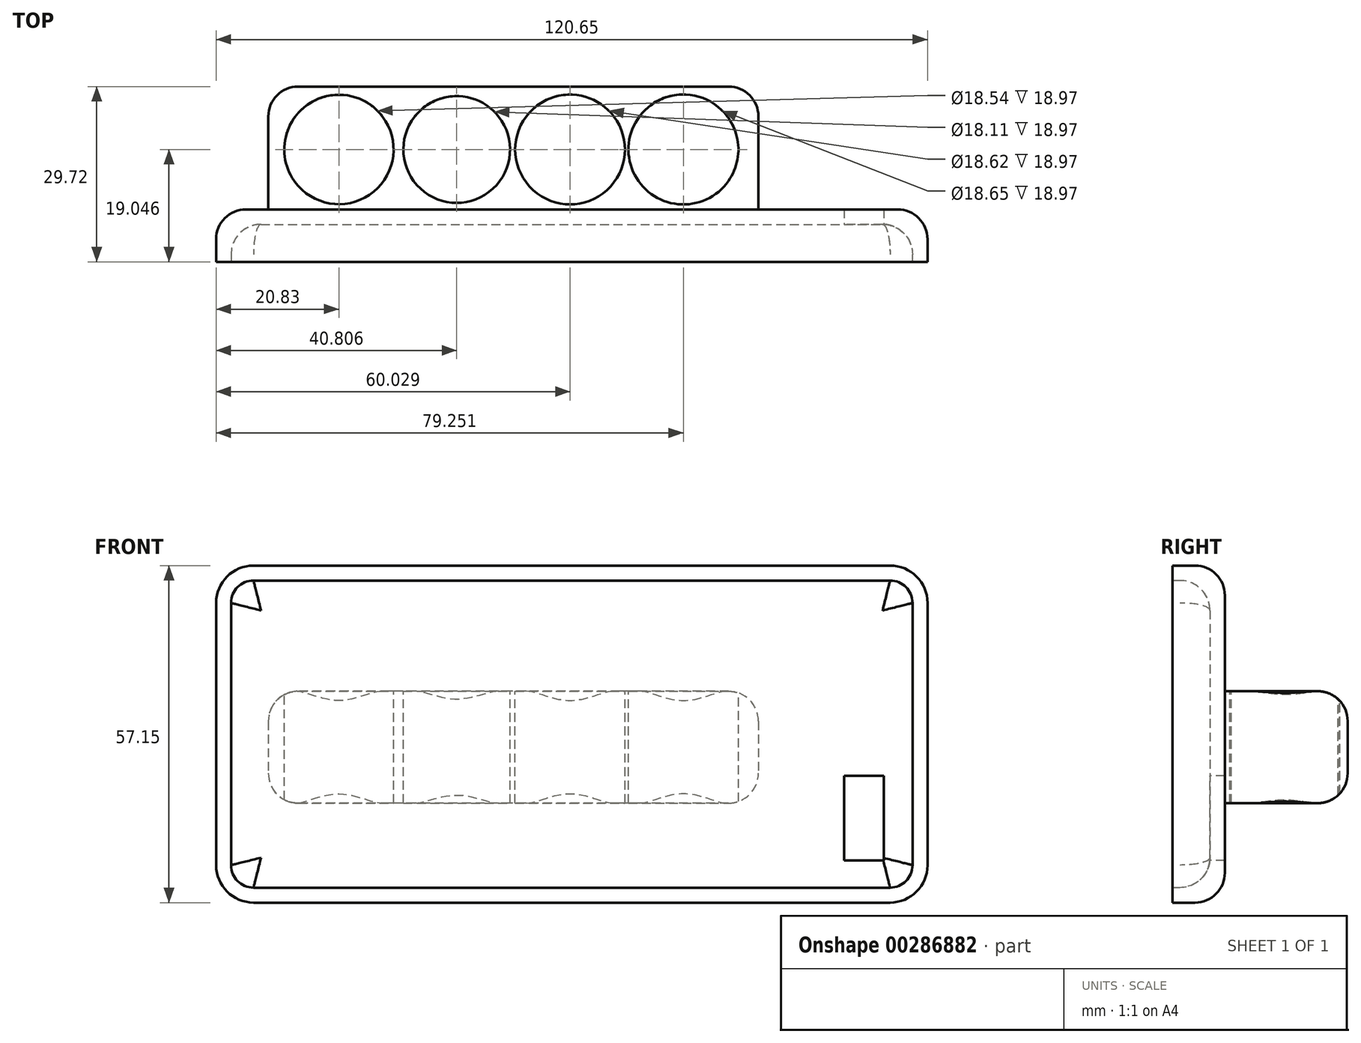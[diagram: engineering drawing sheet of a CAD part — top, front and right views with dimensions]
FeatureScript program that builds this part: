
annotation { "Feature Type Name" : "Feature", "Feature Type Description" : "" }
export const myFeature = defineFeature(function(context is Context, id is Id, definition is map)
    precondition{}
    {
        {
            var Q0;
            Q0=qCreatedBy(makeId("Front.planeOp"),FACE);
            var sketch = newSketch(context, id + "F0", { "sketchPlane" : qUnion([Q0])});
            skLineSegment(sketch, "E0.bottom", {"start": v(-56.78, 40.28) * mm, "end": v(51.17, 40.28) * mm});
            skLineSegment(sketch, "E0.top", {"start": v(-56.78, -16.87) * mm, "end": v(51.17, -16.87) * mm});
            skLineSegment(sketch, "E0.left", {"start": v(-63.13, 33.93) * mm, "end": v(-63.13, -10.52) * mm});
            skLineSegment(sketch, "E0.right", {"start": v(57.52, 33.93) * mm, "end": v(57.52, -10.52) * mm});
            skPoint(sketch, "E1.visualSharp", {"position": v(-63.13, 40.28) * mm});
            skArc(sketch, "E1.filletArc", {"start": v(-56.78, 40.28) * mm, "mid": v(-61.27, 38.42) * mm, "end": v(-63.13, 33.93) * mm});
            skPoint(sketch, "E2.visualSharp", {"position": v(57.52, 40.28) * mm});
            skArc(sketch, "E2.filletArc", {"start": v(57.52, 33.93) * mm, "mid": v(55.66, 38.42) * mm, "end": v(51.17, 40.28) * mm});
            skPoint(sketch, "E3.visualSharp", {"position": v(57.52, -16.87) * mm});
            skArc(sketch, "E3.filletArc", {"start": v(51.17, -16.87) * mm, "mid": v(55.66, -15) * mm, "end": v(57.52, -10.52) * mm});
            skPoint(sketch, "E4.visualSharp", {"position": v(-63.13, -16.87) * mm});
            skArc(sketch, "E4.filletArc", {"start": v(-63.13, -10.52) * mm, "mid": v(-61.27, -15) * mm, "end": v(-56.78, -16.87) * mm});
            skSolve(sketch);
        }
        {
            var Q0;
            Q0=makeQuery(id+"F0.imprint","IMPRINT",FACE,{"disambiguationData":[TD([[makeQuery(id+"F0.imprint","IMPRINT",EDGE,{"derivedFrom":sQuery(id+"F0.wireOp",EDGE,"E0.bottom")}),-1.0]])]});
            extrude(context, id + "F1", {"entities" : qUnion([Q0]), "oppositeDirection" : true, "depth" : 8.9 * mm});
        }
        {
            var Q0;
            Q0=makeQuery(id+"F1.opExtrude","CAP_FACE",FACE,{"disambiguationData":[OSD([sQuery(id+"F0.wireOp",EDGE,"E0.bottom"),sQuery(id+"F0.wireOp",EDGE,"E0.top"),sQuery(id+"F0.wireOp",EDGE,"E0.left"),sQuery(id+"F0.wireOp",EDGE,"E0.right"),sQuery(id+"F0.wireOp",EDGE,"E1.filletArc"),sQuery(id+"F0.wireOp",EDGE,"E2.filletArc"),sQuery(id+"F0.wireOp",EDGE,"E3.filletArc"),sQuery(id+"F0.wireOp",EDGE,"E4.filletArc")])],"isStart":true});
            shell(context, id + "F2", {"entities" : qUnion([Q0]), "thickness" : 2.54 * mm});
        }
        {
            var Q0;
            Q0=qCreatedBy(makeId("Front.planeOp"),FACE);
            var sketch = newSketch(context, id + "F3", { "sketchPlane" : qUnion([Q0])});
            skLineSegment(sketch, "E5.bottom", {"start": v(28.84, 18.97) * mm, "end": v(-54.28, 18.97) * mm});
            skLineSegment(sketch, "E5.top", {"start": v(28.84, 0) * mm, "end": v(-54.28, 0) * mm});
            skLineSegment(sketch, "E5.left", {"start": v(28.84, 18.97) * mm, "end": v(28.84, 0) * mm});
            skLineSegment(sketch, "E5.right", {"start": v(-54.28, 18.97) * mm, "end": v(-54.28, 0) * mm});
            skSolve(sketch);
        }
        {
            var Q0;
            Q0=makeQuery(id+"F3.imprint","IMPRINT",FACE,{"disambiguationData":[TD([[makeQuery(id+"F3.imprint","IMPRINT",EDGE,{"derivedFrom":sQuery(id+"F3.wireOp",EDGE,"E5.bottom")}),1.0]])]});
            extrude(context, id + "F4", {"entities" : qUnion([Q0]), "operationType" : NewBodyOperationType.ADD, "oppositeDirection" : true, "depth" : 29.72 * mm, "hasSecondDirection" : true, "secondDirectionOppositeDirection" : true, "secondDirectionDepth" : 8.13 * mm});
        }
        {
            var Q0;
            Q0=qCreatedBy(makeId("Top.planeOp"),FACE);
            var sketch = newSketch(context, id + "F5", { "sketchPlane" : qUnion([Q0])});
            skCircle(sketch, "E6", {"center": v(16.12, 19.05) * mm, "radius": 9.32 * mm});
            skCircle(sketch, "E7", {"center": v(-3.1, 19.05) * mm, "radius": 9.3 * mm});
            skCircle(sketch, "E8", {"center": v(-22.32, 19.05) * mm, "radius": 9.05 * mm});
            skCircle(sketch, "E9", {"center": v(-42.3, 19.05) * mm, "radius": 9.27 * mm});
            skSolve(sketch);
        }
        {
            var Q0;
            Q0=makeQuery(id+"F5.imprint","IMPRINT",FACE,{"disambiguationData":[TD([[makeQuery(id+"F5.imprint","IMPRINT",EDGE,{"derivedFrom":sQuery(id+"F5.wireOp",EDGE,"E6")}),1.0]])]});
            var Q1;
            Q1=makeQuery(id+"F5.imprint","IMPRINT",FACE,{"disambiguationData":[TD([[makeQuery(id+"F5.imprint","IMPRINT",EDGE,{"derivedFrom":sQuery(id+"F5.wireOp",EDGE,"E7")}),1.0]])]});
            var Q2;
            Q2=makeQuery(id+"F5.imprint","IMPRINT",FACE,{"disambiguationData":[TD([[makeQuery(id+"F5.imprint","IMPRINT",EDGE,{"derivedFrom":sQuery(id+"F5.wireOp",EDGE,"E8")}),1.0]])]});
            var Q3;
            Q3=makeQuery(id+"F5.imprint","IMPRINT",FACE,{"disambiguationData":[TD([[makeQuery(id+"F5.imprint","IMPRINT",EDGE,{"derivedFrom":sQuery(id+"F5.wireOp",EDGE,"E9")}),1.0]])]});
            extrude(context, id + "F6", {"entities" : qUnion([Q0, Q1, Q2, Q3]), "operationType" : NewBodyOperationType.REMOVE, "oppositeDirection" : true, "depth" : 25.4 * mm, "hasSecondDirection" : true, "secondDirectionOppositeDirection" : false, "secondDirectionDepth" : 31.75 * mm});
        }
        {
            var Q0;
            Q0=makeQuery(id+"F4.opExtrude","CAP_EDGE",EDGE,{"disambiguationData":[OSD([sQuery(id+"F3.wireOp",EDGE,"E5.top")])],"isStart":false});
            fillet(context, id + "F7", {"entities" : qUnion([Q0]), "radius" : 5.08 * mm, "tangentPropagation" : true, "allowEdgeOverflow" : false});
        }
        {
            var Q0;
            Q0=makeQuery(id+"F4.opExtrude","CAP_EDGE",EDGE,{"disambiguationData":[OSD([sQuery(id+"F3.wireOp",EDGE,"E5.bottom")])],"isStart":false});
            fillet(context, id + "F8", {"entities" : qUnion([Q0]), "radius" : 5.08 * mm, "tangentPropagation" : true, "allowEdgeOverflow" : false});
        }
        {
            var Q0;
            Q0=makeQuery(id+"F4.opExtrude","CAP_EDGE",EDGE,{"disambiguationData":[OSD([sQuery(id+"F3.wireOp",EDGE,"E5.left")])],"isStart":false});
            fillet(context, id + "F9", {"entities" : qUnion([Q0]), "radius" : 5.08 * mm, "tangentPropagation" : true, "allowEdgeOverflow" : false});
        }
        {
            var Q0;
            Q0=makeQuery(id+"F4.opExtrude","CAP_EDGE",EDGE,{"disambiguationData":[OSD([sQuery(id+"F3.wireOp",EDGE,"E5.right")])],"isStart":false});
            fillet(context, id + "F10", {"entities" : qUnion([Q0]), "radius" : 5.08 * mm, "tangentPropagation" : true, "allowEdgeOverflow" : false});
        }
        {
            var Q0;
            Q0=makeQuery(id+"F1.opExtrude","CAP_EDGE",EDGE,{"disambiguationData":[OSD([sQuery(id+"F0.wireOp",EDGE,"E0.bottom")])],"isStart":false});
            fillet(context, id + "F11", {"entities" : qUnion([Q0]), "radius" : 5.08 * mm, "tangentPropagation" : true, "allowEdgeOverflow" : false});
        }
        {
            var Q0;
            {var subQ0=sQuery(id+"F0.wireOp",EDGE,"E0.bottom");Q0=makeQuery(id+"F2.opShell","OFFSET_EDGE",EDGE,{"disambiguationData":[OSD([subQ0]),TDD([makeQuery(id+"F1.opExtrude","CAP_EDGE",EDGE,{"disambiguationData":[OSD([subQ0])],"isStart":false})])]});}
            fillet(context, id + "F12", {"entities" : qUnion([Q0]), "radius" : 5.08 * mm, "tangentPropagation" : true, "allowEdgeOverflow" : false});
        }
        {
            var Q0;
            Q0=qCreatedBy(makeId("Front.planeOp"),FACE);
            var sketch = newSketch(context, id + "F13", { "sketchPlane" : qUnion([Q0])});
            skLineSegment(sketch, "E10.bottom", {"start": v(50.12, -9.75) * mm, "end": v(43.37, -9.75) * mm});
            skLineSegment(sketch, "E10.top", {"start": v(50.12, 4.66) * mm, "end": v(43.37, 4.66) * mm});
            skLineSegment(sketch, "E10.left", {"start": v(50.12, -9.75) * mm, "end": v(50.12, 4.66) * mm});
            skLineSegment(sketch, "E10.right", {"start": v(43.37, -9.75) * mm, "end": v(43.37, 4.66) * mm});
            skSolve(sketch);
        }
        {
            var Q0;
            Q0=makeQuery(id+"F13.imprint","IMPRINT",FACE,{"disambiguationData":[TD([[makeQuery(id+"F13.imprint","IMPRINT",EDGE,{"derivedFrom":sQuery(id+"F13.wireOp",EDGE,"E10.bottom")}),-1.0]])]});
            extrude(context, id + "F14", {"entities" : qUnion([Q0]), "operationType" : NewBodyOperationType.REMOVE, "oppositeDirection" : true, "depth" : 25.4 * mm});
        }
        {
            var Q0;
            Q0=qCreatedBy(makeId("Right.planeOp"),FACE);
            var sketch = newSketch(context, id + "F15", { "sketchPlane" : qUnion([Q0])});
            skLineSegment(sketch, "E11.bottom", {"start": v(0, -9.62) * mm, "end": v(3.34, -9.62) * mm});
            skLineSegment(sketch, "E11.top", {"start": v(0, 0) * mm, "end": v(3.34, 0) * mm});
            skLineSegment(sketch, "E11.left", {"start": v(0, -9.62) * mm, "end": v(0, 0) * mm});
            skLineSegment(sketch, "E11.right", {"start": v(3.34, -9.62) * mm, "end": v(3.34, 0) * mm});
            skSolve(sketch);
        }
        {
            var Q0;
            Q0=sQuery(id+"F15.wireOp",EDGE,"E11.top");
            var Q1;
            Q1=sQuery(id+"F15.wireOp",EDGE,"E11.right");
            var Q2;
            Q2=sQuery(id+"F15.wireOp",EDGE,"E11.bottom");
            var Q3;
            Q3=sQuery(id+"F15.wireOp",EDGE,"E11.left");
            extrude(context, id + "F16", {"bodyType" : ToolBodyType.SURFACE, "surfaceEntities" : qUnion([Q0, Q1, Q2, Q3]), "depth" : 58.67 * mm, "hasSecondDirection" : true, "secondDirectionOppositeDirection" : false, "secondDirectionDepth" : 54.36 * mm});
        }
    });
